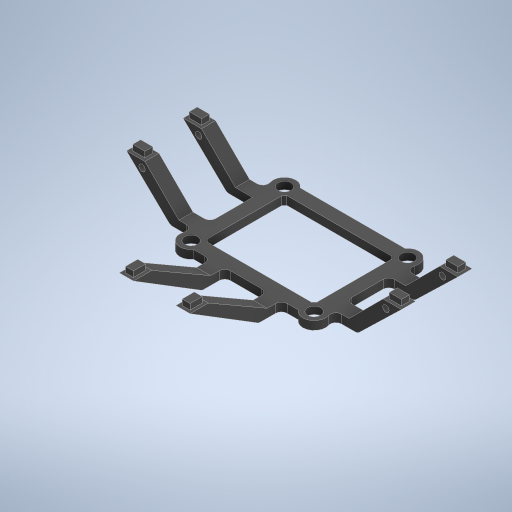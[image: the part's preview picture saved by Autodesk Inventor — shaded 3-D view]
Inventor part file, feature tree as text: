
AUTODESK INVENTOR PART (.ipt)
format: ipt  version: 2024.2 (Build 282272000, 272)  size: 489,472 bytes
history: native  units: mm
features: extrude x6, sketch x6, mirror x5, plane x4, fillet x2, chamfer x1
ambient origin geometry x8: Origin, YZ Plane, XZ Plane, XY Plane, X Axis, Y Axis, Z Axis, Center Point
bodies: Solid1 (feature_tree)
feature tree (24):
  extrude  "Extrusion1"  Depth=8.0mm
  chamfer  "Chamfer1"  Distance=8.0mm
  plane  "Work Plane2"
  extrude  "Extrusion2"  Depth=4.0mm
  plane  "Work Plane4"
  plane  "Work Plane5"
  mirror  "Mirror1"
  mirror  "Mirror2"
  plane  "Work Plane6"
  extrude  "Extrusion5"  Depth=4.0mm
  mirror  "Mirror5"
  extrude  "Extrusion4"  Depth=4.0mm
  mirror  "Mirror3"
  mirror  "Mirror4"
  extrude  "Extrusion6"  Depth=4.0mm
  fillet  "Fillet1"  Radius=4.0mm
  fillet  "Fillet2"  Radius=4.0mm
  extrude  "Extrusion8"  Depth=4.0mm
  sketch  "Sketch1"  dims[d0=4.7mm d1=8.0mm]
  sketch  "Sketch2"  dims[d2=4.7mm]
  sketch  "Sketch5"  dims[d3=8.0mm]
  sketch  "Sketch7"  dims[d4=4.7mm]
  sketch  "Sketch8"  dims[d5=8.0mm]
  sketch  "Sketch11"  dims[d6=4.7mm d7=8.0mm d8=4.0mm d9=4.0mm d10=4.0mm d11=4.0mm d12=4.0mm d13=4.0mm d14=4.0mm d15=4.0mm d16=33.0mm d17=4.7mm d18=4.7mm d19=4.7mm d20=4.7mm d21=2.35mm d22=2.35mm d23=2.35mm d24=2.35mm d25=43.5mm d26=3.0mm d27=0.0mm d28=0.5mm d29=2.0mm d30=45.0deg d32=4.0mm d41=5.0mm d42=0.0mm d47=21.75mm d48=16.5mm d49=6.5mm d61=9.0mm d62=4.3mm d63=2.8mm d64=1.1mm d65=1.1mm d66=2.0mm d67=0.0mm d71=9.25mm d72=8.0mm d73=6.5mm d76=5.0mm d77=0.0mm d78=2.8mm d79=4.3mm d80=2.8mm d81=4.3mm d82=1.1mm d83=1.1mm d84=1.1mm d85=1.1mm d86=2.0mm d87=0.0mm d91=6.0mm d93=45.0deg d94=15.0mm d95=15.0mm d96=2.0mm d97=2.0mm d98=5.0mm d99=30.0deg d105=2.3mm d106=2.5mm d107=5.5mm d108=2.3mm d109=2.5mm d110=5.5mm d111=0.0mm d112=0.0mm]
